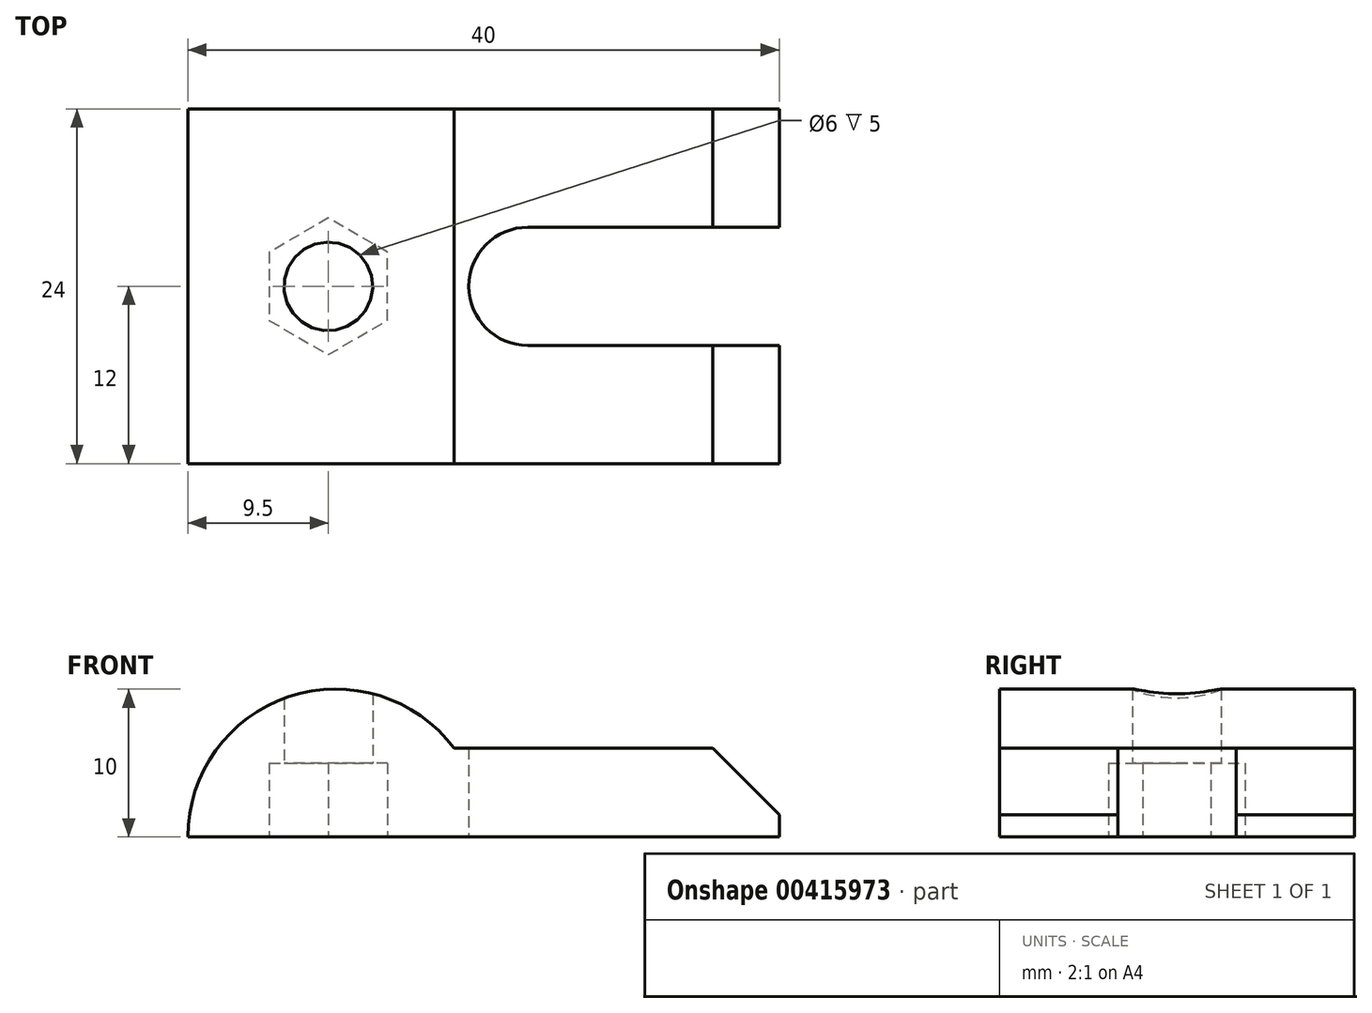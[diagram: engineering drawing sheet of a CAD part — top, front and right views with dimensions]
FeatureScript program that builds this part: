
annotation { "Feature Type Name" : "Feature", "Feature Type Description" : "" }
export const myFeature = defineFeature(function(context is Context, id is Id, definition is map)
    precondition{}
    {
        {
            var Q0;
            Q0=qCreatedBy(makeId("Top.planeOp"),FACE);
            var sketch = newSketch(context, id + "F0", { "sketchPlane" : qUnion([Q0])});
            skLineSegment(sketch, "E0.bottom", {"start": v(0, 0) * mm, "end": v(40, 0) * mm});
            skLineSegment(sketch, "E0.top", {"start": v(0, 24) * mm, "end": v(40, 24) * mm});
            skLineSegment(sketch, "E0.left", {"start": v(0, 0) * mm, "end": v(0, 24) * mm});
            skLineSegment(sketch, "E0.right", {"start": v(40, 0) * mm, "end": v(40, 24) * mm});
            skLineSegment(sketch, "E1", {"start": v(-7.37, 12) * mm, "end": v(58.59, 12) * mm, "construction": true});
            skPoint(sketch, "E1.startSnap0", {"position": v(0, 12) * mm});
            skPoint(sketch, "E1.endSnap0", {"position": v(0, 12) * mm});
            skLineSegment(sketch, "E2", {"start": v(23, 16) * mm, "end": v(40, 16) * mm});
            skLineSegment(sketch, "E3", {"start": v(23, 8) * mm, "end": v(40, 8) * mm});
            skArc(sketch, "E4", {"start": v(23, 16) * mm, "mid": v(19, 12) * mm, "end": v(23, 8) * mm});
            skCircle(sketch, "E5", {"center": v(9.5, 12) * mm, "radius": 3 * mm});
            skSolve(sketch);
        }
        {
            var Q0;
            {var subQ4=sQuery(id+"F0.wireOp",EDGE,"E0.bottom");Q0=makeQuery(id+"F0.imprint","IMPRINT",FACE,{"disambiguationData":[TD([[makeQuery(id+"F0.imprint","IMPRINT",EDGE,{"derivedFrom":subQ4}),1.0]])]});}
            extrude(context, id + "F1", {"entities" : qUnion([Q0]), "depth" : 10 * mm});
        }
        {
            var Q0;
            Q0=makeQuery(id+"F1.opExtrude","CAP_FACE",FACE,{"disambiguationData":[OSD([sQuery(id+"F0.wireOp",EDGE,"E0.bottom"),sQuery(id+"F0.wireOp",EDGE,"E0.top"),sQuery(id+"F0.wireOp",EDGE,"E0.left"),sQuery(id+"F0.wireOp",EDGE,"E0.right"),sQuery(id+"F0.wireOp",EDGE,"E2"),sQuery(id+"F0.wireOp",EDGE,"E3"),sQuery(id+"F0.wireOp",EDGE,"E4"),sQuery(id+"F0.wireOp",EDGE,"E5")])],"isStart":true});
            var sketch = newSketch(context, id + "F2", { "sketchPlane" : qUnion([Q0])});
            skCircle(sketch, "E6.cCircle", {"center": v(9.5, -12) * mm, "radius": 4.62 * mm, "construction": true});
            skLineSegment(sketch, "E6.0", {"start": v(13.5, -14.3) * mm, "end": v(9.5, -16.62) * mm});
            skLineSegment(sketch, "E6.1", {"start": v(9.5, -16.62) * mm, "end": v(5.5, -14.3) * mm});
            skLineSegment(sketch, "E6.2", {"start": v(5.5, -14.3) * mm, "end": v(5.5, -9.7) * mm});
            skLineSegment(sketch, "E6.3", {"start": v(5.5, -9.7) * mm, "end": v(9.5, -7.38) * mm});
            skLineSegment(sketch, "E6.4", {"start": v(9.5, -7.38) * mm, "end": v(13.5, -9.7) * mm});
            skLineSegment(sketch, "E6.5", {"start": v(13.5, -9.7) * mm, "end": v(13.5, -14.3) * mm});
            skSolve(sketch);
        }
        {
            var Q0;
            Q0=makeQuery(id+"F2.imprint","IMPRINT",FACE,{"disambiguationData":[TD([[makeQuery(id+"F2.imprint","IMPRINT",EDGE,{"derivedFrom":sQuery(id+"F2.wireOp",EDGE,"E6.0")}),-1.0]])]});
            extrude(context, id + "F3", {"entities" : qUnion([Q0]), "operationType" : NewBodyOperationType.REMOVE, "oppositeDirection" : true, "depth" : 5 * mm});
        }
        {
            var Q0;
            Q0=makeQuery(id+"F1.opExtrude","SWEPT_FACE",FACE,{"disambiguationData":[OSD([sQuery(id+"F0.wireOp",EDGE,"E0.bottom")])]});
            var sketch = newSketch(context, id + "F4", { "sketchPlane" : qUnion([Q0])});
            skLineSegment(sketch, "E7", {"start": v(40, 0) * mm, "end": v(40, 1.5) * mm});
            skLineSegment(sketch, "E8", {"start": v(40, 1.5) * mm, "end": v(35.5, 6) * mm});
            skLineSegment(sketch, "E9", {"start": v(35.5, 6) * mm, "end": v(18, 6) * mm});
            skArc(sketch, "E10", {"start": v(18, 6) * mm, "mid": v(6.84, 9.49) * mm, "end": v(0, 0) * mm});
            skSolve(sketch);
        }
        {
            var Q0;
            {var subQ1=sQuery(id+"F0.wireOp",EDGE,"E0.bottom");var subQ2=makeQuery(id+"F1.opExtrude","SWEPT_EDGE",EDGE,{"disambiguationData":[OSD([subQ1,sQuery(id+"F0.wireOp",EDGE,"E0.left")])]});Q0=makeQuery(id+"F4.imprint","IMPRINT",FACE,{"disambiguationData":[TD([[makeQuery(id+"F4.imprint","IMPRINT",EDGE,{"derivedFrom":subQ2}),1.0]])]});}
            var Q1;
            {var subQ7=sQuery(id+"F4.wireOp",EDGE,"E8");Q1=makeQuery(id+"F4.imprint","IMPRINT",FACE,{"disambiguationData":[TD([[makeQuery(id+"F4.imprint","IMPRINT",EDGE,{"derivedFrom":subQ7}),-1.0]])]});}
            extrude(context, id + "F5", {"entities" : qUnion([Q0, Q1]), "operationType" : NewBodyOperationType.REMOVE, "endBound" : BoundingType.THROUGH_ALL, "oppositeDirection" : true, "depth" : 25 * mm});
        }
    });
